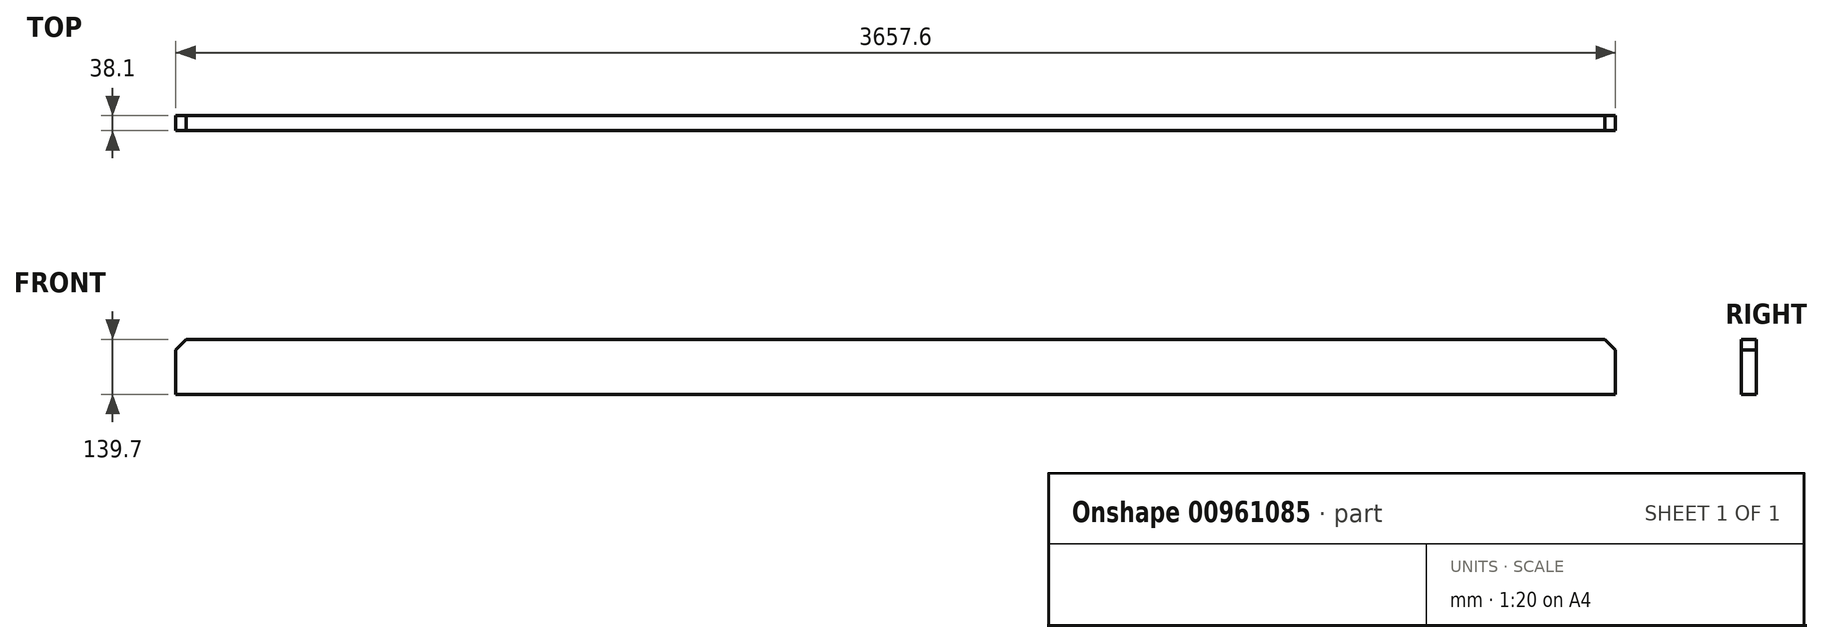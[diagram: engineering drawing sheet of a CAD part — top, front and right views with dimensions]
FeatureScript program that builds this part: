
annotation { "Feature Type Name" : "Feature", "Feature Type Description" : "" }
export const myFeature = defineFeature(function(context is Context, id is Id, definition is map)
    precondition{}
    {
        {
            var Q0;
            Q0=qCreatedBy(makeId("Front.planeOp"),FACE);
            var sketch = newSketch(context, id + "F0", { "sketchPlane" : qUnion([Q0])});
            skLineSegment(sketch, "E0.bottom", {"start": v(1828.8, -69.85) * mm, "end": v(-1828.8, -69.85) * mm});
            skLineSegment(sketch, "E0.top", {"start": v(1801.86, 69.85) * mm, "end": v(-1801.86, 69.85) * mm});
            skLineSegment(sketch, "E0.left", {"start": v(1828.8, -69.85) * mm, "end": v(1828.8, 42.9) * mm});
            skLineSegment(sketch, "E0.right", {"start": v(-1828.8, -69.85) * mm, "end": v(-1828.8, 42.9) * mm});
            skPoint(sketch, "E0.middle", {"position": v(0, 0) * mm});
            skLineSegment(sketch, "E1", {"start": v(-1828.8, 42.9) * mm, "end": v(-1801.86, 69.85) * mm});
            skLineSegment(sketch, "E2.MirrorCS", {"start": v(1828.8, 42.9) * mm, "end": v(1801.86, 69.85) * mm});
            skPoint(sketch, "E3.orphan", {"position": v(-1828.8, 69.85) * mm});
            skPoint(sketch, "E4.orphan", {"position": v(1828.8, 69.85) * mm});
            skSolve(sketch);
        }
        {
            var Q0;
            Q0=makeQuery(id+"F0.imprint","IMPRINT",FACE,{"disambiguationData":[TD([[makeQuery(id+"F0.imprint","IMPRINT",EDGE,{"derivedFrom":sQuery(id+"F0.wireOp",EDGE,"E0.bottom")}),-1.0]])]});
            extrude(context, id + "F1", {"entities" : qUnion([Q0]), "depth" : 38.1 * mm, "offsetDistance" : 25.4 * mm});
        }
    });
